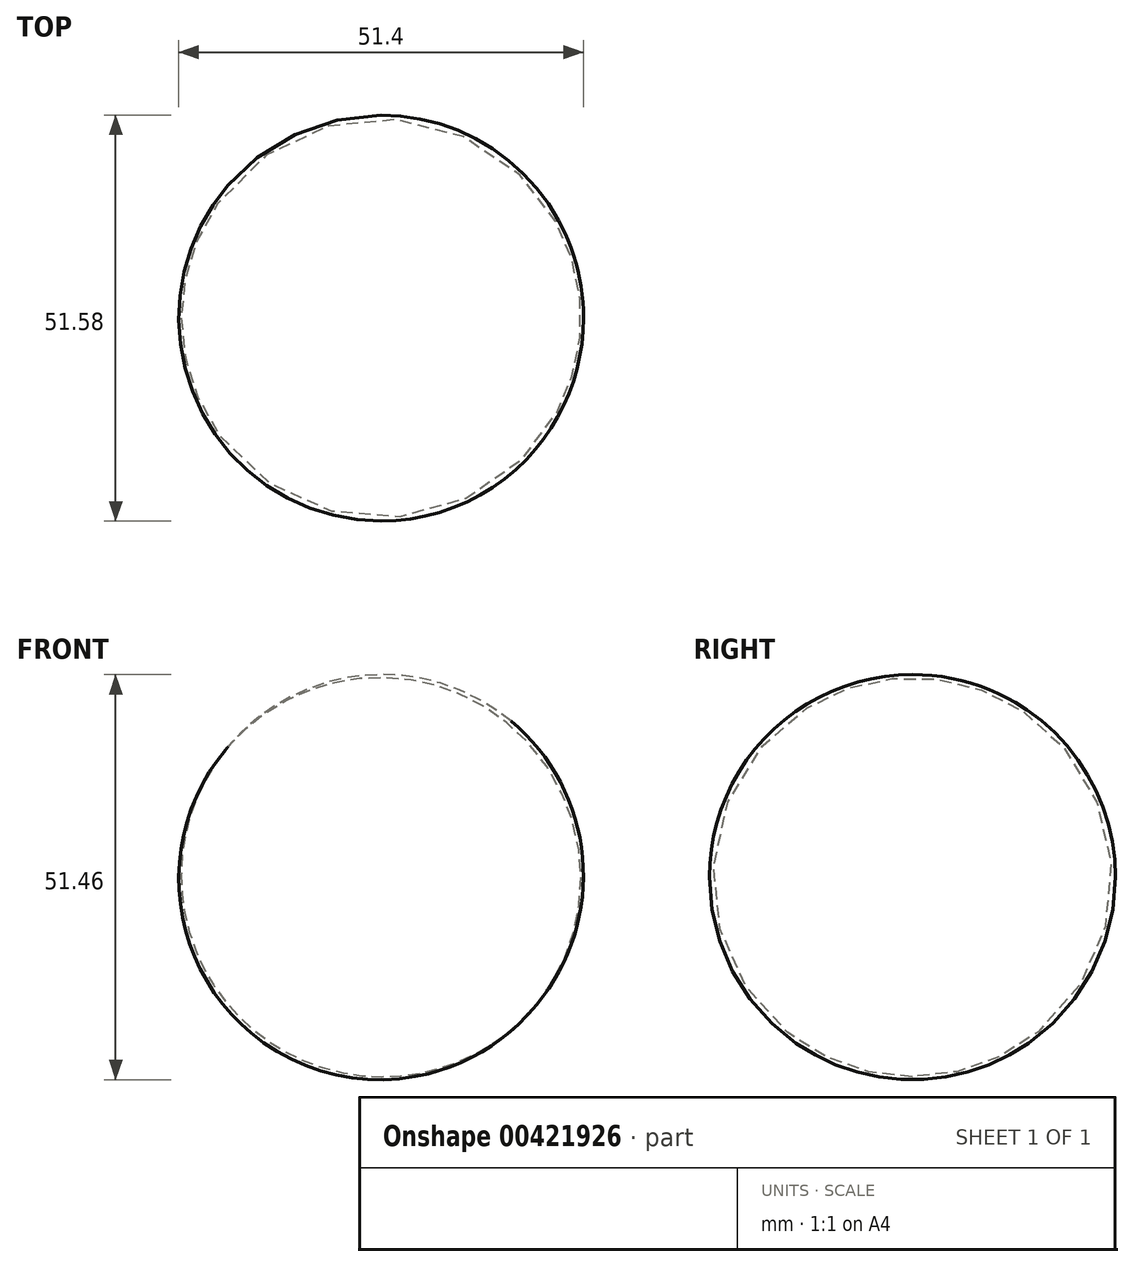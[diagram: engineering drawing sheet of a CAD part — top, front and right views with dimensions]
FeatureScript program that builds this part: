
annotation { "Feature Type Name" : "Feature", "Feature Type Description" : "" }
export const myFeature = defineFeature(function(context is Context, id is Id, definition is map)
    precondition{}
    {
        {
            var Q0;
            Q0=qCreatedBy(makeId("Front.planeOp"),FACE);
            var sketch = newSketch(context, id + "F0", { "sketchPlane" : qUnion([Q0])});
            skArc(sketch, "E0", {"start": v(-19.47, 16.54) * mm, "mid": v(-16.35, -19.63) * mm, "end": v(19.78, -16.15) * mm});
            skLineSegment(sketch, "E1", {"start": v(-19.47, 16.54) * mm, "end": v(19.78, -16.15) * mm});
            skSolve(sketch);
        }
        {
            var Q0;
            Q0=makeQuery(id+"F0.imprint","IMPRINT",FACE,{"disambiguationData":[TD([[makeQuery(id+"F0.imprint","IMPRINT",EDGE,{"derivedFrom":sQuery(id+"F0.wireOp",EDGE,"E0")}),1.0]])]});
            var Q1;
            Q1=sQuery(id+"F0.wireOp",EDGE,"E1");
            revolve(context, id + "F1", {"entities" : qUnion([Q0]), "axis" : qUnion([Q1]), "revolveType" : RevolveType.FULL});
        }
    });
